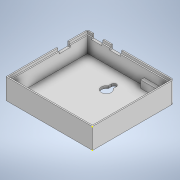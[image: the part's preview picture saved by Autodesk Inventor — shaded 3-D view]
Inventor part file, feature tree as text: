
AUTODESK INVENTOR PART (.ipt)
format: ipt  version: 2022 (Build 260153000, 153)  size: 226,816 bytes
history: native  units: in
note: dims shown in document units (in); Inventor stores cm internally (conversion verified against a paired STEP export)
features: sketch x9, extrude x7, fillet x2
ambient origin geometry x8: Origin, YZ Plane, XZ Plane, XY Plane, X Axis, Y Axis, Z Axis, Center Point
bodies: Solid1 (feature_tree)
feature tree (18):
  sketch  "Sketch1"  dims[d0=2.7559in d1=2.5984in]
  extrude  "Extrusion1"  Depth=2.5984in
  sketch  "Sketch3"  dims[d6=0.0787in d7=0.0787in]
  extrude  "Extrusion2"  Depth=0.0787in
  extrude  "Extrusion5"  Depth=0.0787in
  extrude  "Extrusion7"  Depth=0.0787in
  extrude  "Extrusion8"  Depth=0.0787in
  extrude  "Extrusion9"  Depth=0.5807in TaperAngle=0.0deg
  extrude  "Extrusion10"  Depth=0.5906in
  fillet  "Fillet7"  Radius=0.5906in
  fillet  "Fillet8"  Radius=0.2362in
  sketch  "Sketch2"  dims[d2=0.6594in d3=0.0in d5=0.0787in]
  sketch  "Sketch4"  dims[d8=0.0787in d9=0.0787in]
  sketch  "Sketch10"  dims[d10=0.0787in d11=0.0787in]
  sketch  "Sketch12"  dims[d12=0.0787in d13=0.5807in d14=0.0in]
  sketch  "Sketch13"  dims[d55=0.1181in d56=0.5906in d60=0.5906in d64=0.2362in d65=0.0in]
  sketch  "Sketch15"  dims[d79=0.1969in d80=0.0in]
  sketch  "Sketch16"  dims[d88=0.0787in d89=0.0in d94=0.0394in d95=0.0394in d96=0.0394in d97=0.0394in d98=0.0394in d99=0.0394in d100=0.0394in d101=0.0394in d102=0.0787in d103=0.0787in d104=0.0787in d108=0.1181in d118=0.315in d125=0.3937in d126=0.0in d127=0.3346in d128=0.3346in d129=0.1378in d130=0.2087in d131=1.126in d132=0.5315in d133=0.3937in d134=0.0in d140=0.9843in d141=0.3543in d142=0.1378in d143=0.1969in d144=0.0787in d145=0.0787in d40=0.0197in d41=0.0344in d42=0.0197in d43=0.0344in d66=0.0197in d67=0.0344in d74=0.0197in d75=0.0344in d76=0.0197in d77=0.0344in d115=0.0in d116=0.0in d117=0.0in d135=0.0197in d136=0.0344in d137=0.0197in d138=0.0344in d148=0.0in d149=0.0in d150=0.0in d151=0.0in]
